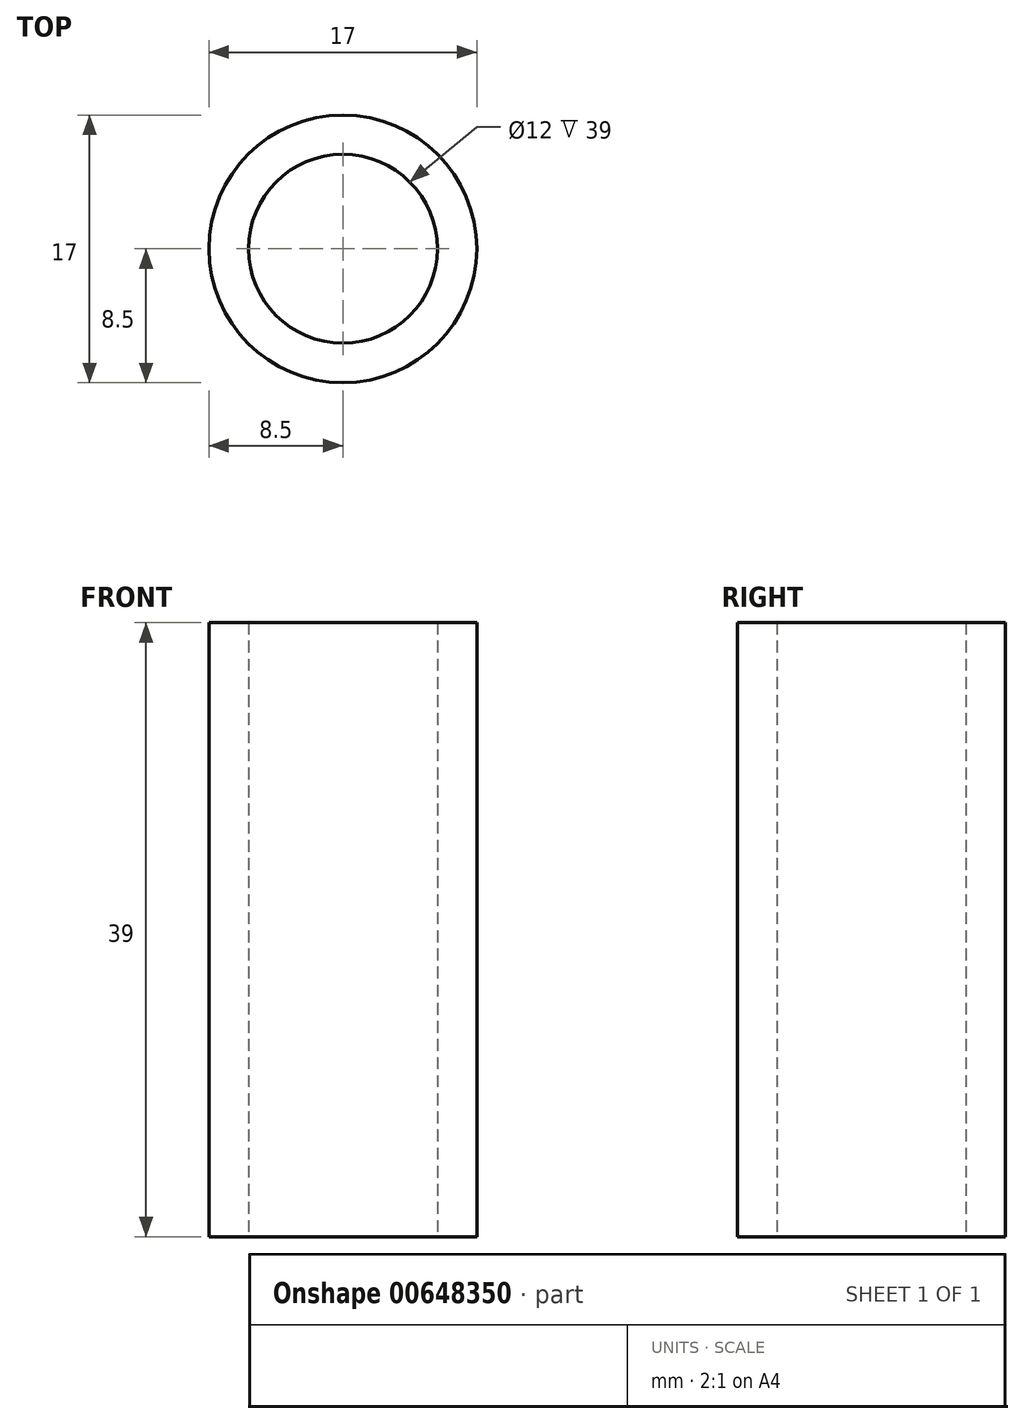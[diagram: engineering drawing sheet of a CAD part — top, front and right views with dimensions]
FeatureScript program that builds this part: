
annotation { "Feature Type Name" : "Feature", "Feature Type Description" : "" }
export const myFeature = defineFeature(function(context is Context, id is Id, definition is map)
    precondition{}
    {
        {
            var Q0;
            Q0=qCreatedBy(makeId("Top.planeOp"),FACE);
            var sketch = newSketch(context, id + "F0", { "sketchPlane" : qUnion([Q0])});
            skCircle(sketch, "E0", {"center": v(0, 0) * mm, "radius": 6 * mm});
            skCircle(sketch, "E1", {"center": v(0, 0) * mm, "radius": 8.5 * mm});
            skSolve(sketch);
        }
        {
            var Q0;
            Q0 = qSketchRegion(id + "F0", true);
            extrude(context, id + "F1", {"entities" : qUnion([Q0]), "depth" : 39 * mm, "offsetDistance" : 25 * mm});
        }
    });
